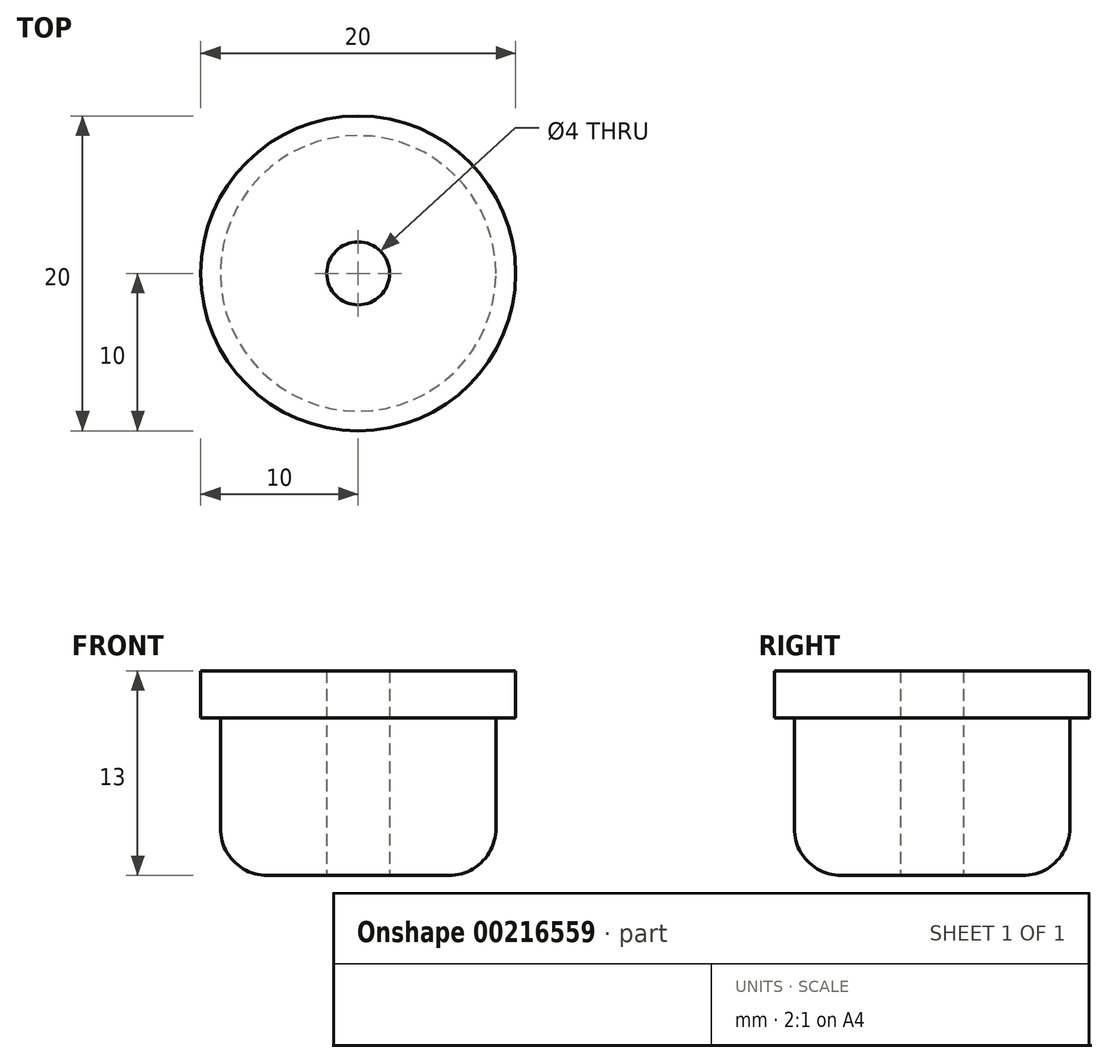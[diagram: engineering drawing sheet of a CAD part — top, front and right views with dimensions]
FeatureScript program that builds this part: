
annotation { "Feature Type Name" : "Feature", "Feature Type Description" : "" }
export const myFeature = defineFeature(function(context is Context, id is Id, definition is map)
    precondition{}
    {
        {
            var Q0;
            Q0=qCreatedBy(makeId("Top.planeOp"),FACE);
            var sketch = newSketch(context, id + "F0", { "sketchPlane" : qUnion([Q0])});
            skCircle(sketch, "E0", {"center": v(0, 0) * mm, "radius": 10 * mm});
            skSolve(sketch);
        }
        {
            var Q0;
            Q0=makeQuery(id+"F0.imprint","IMPRINT",FACE,{"disambiguationData":[TD([[makeQuery(id+"F0.imprint","IMPRINT",EDGE,{"derivedFrom":sQuery(id+"F0.wireOp",EDGE,"E0")}),1.0]])]});
            var Q1;
            Q1=sQuery(id+"F0.wireOp",EDGE,"E0");
            extrude(context, id + "F1", {"entities" : qUnion([Q0]), "surfaceEntities" : qUnion([Q1]), "depth" : 3 * mm});
        }
        {
            var Q0;
            Q0=makeQuery(id+"F1.opExtrude","CAP_FACE",FACE,{"disambiguationData":[OSD([sQuery(id+"F0.wireOp",EDGE,"E0")])],"isStart":true});
            var sketch = newSketch(context, id + "F2", { "sketchPlane" : qUnion([Q0])});
            skCircle(sketch, "E1", {"center": v(0, 0) * mm, "radius": 8.75 * mm});
            skSolve(sketch);
        }
        {
            var Q0;
            Q0=makeQuery(id+"F2.imprint","IMPRINT",FACE,{"disambiguationData":[TD([[makeQuery(id+"F2.imprint","IMPRINT",EDGE,{"derivedFrom":sQuery(id+"F2.wireOp",EDGE,"E1")}),1.0]])]});
            var Q1;
            Q1=sQuery(id+"F2.wireOp",EDGE,"E1");
            extrude(context, id + "F3", {"entities" : qUnion([Q0]), "operationType" : NewBodyOperationType.ADD, "surfaceEntities" : qUnion([Q1]), "depth" : 10 * mm});
        }
        {
            var Q0;
            Q0=makeQuery(id+"F3.opExtrude","CAP_EDGE",EDGE,{"disambiguationData":[OSD([sQuery(id+"F2.wireOp",EDGE,"E1")])],"isStart":false});
            fillet(context, id + "F4", {"entities" : qUnion([Q0]), "radius" : 3 * mm, "tangentPropagation" : true, "allowEdgeOverflow" : false});
        }
        {
            var Q0;
            Q0=makeQuery(id+"F3.opExtrude","CAP_FACE",FACE,{"disambiguationData":[OSD([sQuery(id+"F2.wireOp",EDGE,"E1")])],"isStart":false});
            var sketch = newSketch(context, id + "F5", { "sketchPlane" : qUnion([Q0])});
            skCircle(sketch, "E2", {"center": v(0, 0) * mm, "radius": 1.57 * mm});
            skSolve(sketch);
        }
        {
            var Q0;
            Q0=sQuery(id+"F5.wireOp",VERTEX,"E2.center");
            var Q1;
            Q1=makeQuery(id+"F1.opExtrude","SWEPT_BODY",BODY,{"disambiguationData":[OSD([sQuery(id+"F0.wireOp",EDGE,"E0")])]});
            hole(context, id + "F6", {"style" : HoleStyle.SIMPLE, "endStyle" : HoleEndStyle.THROUGH, "holeDiameter" : 4 * mm, "locations" : qUnion([Q0]), "scope" : qUnion([Q1]), "isTappedThrough" : true});
        }
    });
